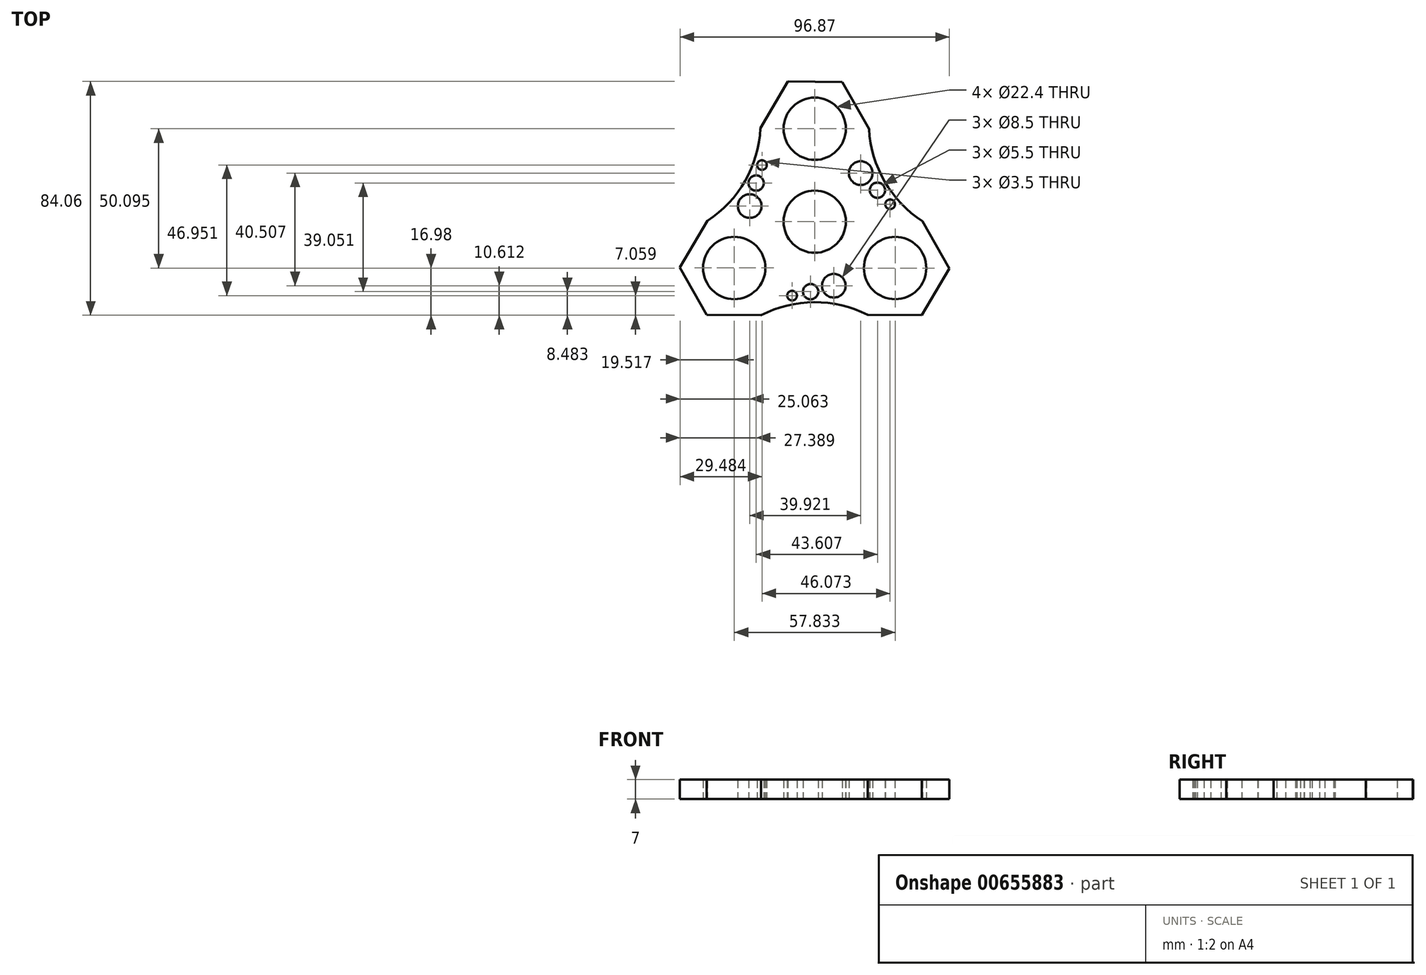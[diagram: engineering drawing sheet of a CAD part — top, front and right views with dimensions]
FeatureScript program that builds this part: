
annotation { "Feature Type Name" : "Feature", "Feature Type Description" : "" }
export const myFeature = defineFeature(function(context is Context, id is Id, definition is map)
    precondition{}
    {
        {
            var Q0;
            Q0=qCreatedBy(makeId("Top.planeOp"),FACE);
            var sketch = newSketch(context, id + "F0", { "sketchPlane" : qUnion([Q0])});
            skCircle(sketch, "E0", {"center": v(0, 0) * mm, "radius": 11.2 * mm});
            skCircle(sketch, "E1.cCircle", {"center": v(0, 33.41) * mm, "radius": 16.9 * mm, "construction": true});
            skLineSegment(sketch, "E1.0", {"start": v(9.9, 50.24) * mm, "end": v(19.52, 33.26) * mm});
            skLineSegment(sketch, "E1.1", {"start": v(19.52, 33.26) * mm, "end": v(9.63, 16.43) * mm});
            skLineSegment(sketch, "E1.2", {"start": v(9.63, 16.43) * mm, "end": v(-9.9, 16.59) * mm});
            skLineSegment(sketch, "E1.3", {"start": v(-9.9, 16.59) * mm, "end": v(-19.52, 33.57) * mm});
            skLineSegment(sketch, "E1.4", {"start": v(-19.52, 33.57) * mm, "end": v(-9.63, 50.4) * mm});
            skLineSegment(sketch, "E1.5", {"start": v(-9.63, 50.4) * mm, "end": v(9.9, 50.24) * mm});
            skPoint(sketch, "E1.0.midPoint", {"position": v(14.7, 41.75) * mm});
            skCircle(sketch, "E2", {"center": v(0, 33.41) * mm, "radius": 11.2 * mm});
            skCircle(sketch, "E3.1.0", {"center": v(-28.93, -16.66) * mm, "radius": 11.2 * mm});
            skLineSegment(sketch, "E3.1.1", {"start": v(-48.45, -16.5) * mm, "end": v(-38.56, 0.32) * mm});
            skLineSegment(sketch, "E3.1.2", {"start": v(-38.56, 0.32) * mm, "end": v(-19.04, 0.17) * mm});
            skLineSegment(sketch, "E3.1.3", {"start": v(-19.04, 0.17) * mm, "end": v(-9.41, -16.81) * mm});
            skLineSegment(sketch, "E3.1.4", {"start": v(-9.41, -16.81) * mm, "end": v(-19.3, -33.64) * mm});
            skLineSegment(sketch, "E3.1.5", {"start": v(-19.3, -33.64) * mm, "end": v(-38.83, -33.5) * mm});
            skLineSegment(sketch, "E3.1.6", {"start": v(-38.83, -33.5) * mm, "end": v(-48.45, -16.5) * mm});
            skCircle(sketch, "E3.1.7", {"center": v(-28.93, -16.66) * mm, "radius": 16.9 * mm, "construction": true});
            skCircle(sketch, "E3.2.0", {"center": v(28.9, -16.68) * mm, "radius": 11.2 * mm});
            skLineSegment(sketch, "E3.2.1", {"start": v(38.53, -33.66) * mm, "end": v(19, -33.5) * mm});
            skLineSegment(sketch, "E3.2.2", {"start": v(19, -33.5) * mm, "end": v(9.38, -16.53) * mm});
            skLineSegment(sketch, "E3.2.3", {"start": v(9.38, -16.53) * mm, "end": v(19.27, 0.3) * mm});
            skLineSegment(sketch, "E3.2.4", {"start": v(19.27, 0.3) * mm, "end": v(38.8, 0.15) * mm});
            skLineSegment(sketch, "E3.2.5", {"start": v(38.8, 0.15) * mm, "end": v(48.42, -16.83) * mm});
            skLineSegment(sketch, "E3.2.6", {"start": v(48.42, -16.83) * mm, "end": v(38.53, -33.66) * mm});
            skCircle(sketch, "E3.2.7", {"center": v(28.9, -16.68) * mm, "radius": 16.9 * mm, "construction": true});
            skPoint(sketch, "E3.center", {"position": v(-0.01, 0.02) * mm});
            skArc(sketch, "E4", {"start": v(9.63, 16.43) * mm, "mid": v(9.92, 5.66) * mm, "end": v(19.27, 0.3) * mm});
            skArc(sketch, "E5", {"start": v(9.38, -16.53) * mm, "mid": v(-0.1, -11.4) * mm, "end": v(-9.41, -16.81) * mm});
            skArc(sketch, "E6", {"start": v(-19.04, 0.17) * mm, "mid": v(-9.85, 5.8) * mm, "end": v(-9.9, 16.59) * mm});
            skArc(sketch, "E7", {"start": v(19.52, 33.26) * mm, "mid": v(25.16, 14.38) * mm, "end": v(38.8, 0.15) * mm});
            skArc(sketch, "E8", {"start": v(-38.56, 0.32) * mm, "mid": v(-25.03, 14.65) * mm, "end": v(-19.52, 33.57) * mm});
            skArc(sketch, "E9", {"start": v(19, -33.5) * mm, "mid": v(-0.17, -28.95) * mm, "end": v(-19.3, -33.64) * mm});
            skCircle(sketch, "E10", {"center": v(16.53, 17.46) * mm, "radius": 4.25 * mm});
            skCircle(sketch, "E11", {"center": v(22.55, 11.3) * mm, "radius": 2.75 * mm});
            skCircle(sketch, "E12", {"center": v(27.1, 6.25) * mm, "radius": 1.75 * mm});
            skCircle(sketch, "E13.1.0", {"center": v(-23.39, 5.59) * mm, "radius": 4.25 * mm});
            skCircle(sketch, "E13.1.1", {"center": v(-21.06, 13.87) * mm, "radius": 2.75 * mm});
            skCircle(sketch, "E13.1.2", {"center": v(-18.97, 20.35) * mm, "radius": 1.75 * mm});
            skCircle(sketch, "E13.2.0", {"center": v(6.85, -23.05) * mm, "radius": 4.25 * mm});
            skCircle(sketch, "E13.2.1", {"center": v(-1.48, -25.18) * mm, "radius": 2.75 * mm});
            skCircle(sketch, "E13.2.2", {"center": v(-8.14, -26.6) * mm, "radius": 1.75 * mm});
            skSolve(sketch);
        }
        {
            var Q0;
            Q0 = qSketchRegion(id + "F0", true);
            var Q1;
            Q1=makeQuery(id+"F0.imprint","IMPRINT",FACE,{"disambiguationData":[TD([[makeQuery(id+"F0.imprint","IMPRINT",EDGE,{"derivedFrom":sQuery(id+"F0.wireOp",EDGE,"E0")}),-1.0]])]});
            extrude(context, id + "F1", {"entities" : qUnion([Q0, Q1]), "depth" : 7 * mm, "offsetDistance" : 25 * mm});
        }
    });
